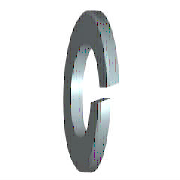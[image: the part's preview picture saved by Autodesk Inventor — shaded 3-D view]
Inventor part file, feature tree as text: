
AUTODESK INVENTOR PART (.ipt)
format: ipt  version: 2024 (Build 280153000, 153)  size: 125,440 bytes
history: native  units: mm (DEFAULTED — no unit token found)
features: sketch x2, extrude x1, other x1, plane x1
ambient origin geometry x6: Origin, YZ Plane, X Axis, Y Axis, Z Axis, Center Point
bodies: Solid1 (feature_tree), Body (feature_tree)
feature tree (5):
  extrude  "Cut"  Depth=5.2mm
  other  "Work Axis1"
  plane  "Work Plane1"
  sketch  "Sketch1"  dims[d0=3.5mm d1=5.2mm]
  sketch  "Sketch2"  dims[d2=1.0mm d3=0.0mm d4=0.2mm d5=0.2mm d6=60.0deg d7=1.0mm d8=0.0mm d9=0.0mm d10=0.0mm d11=0.0mm d12=0.0mm]
